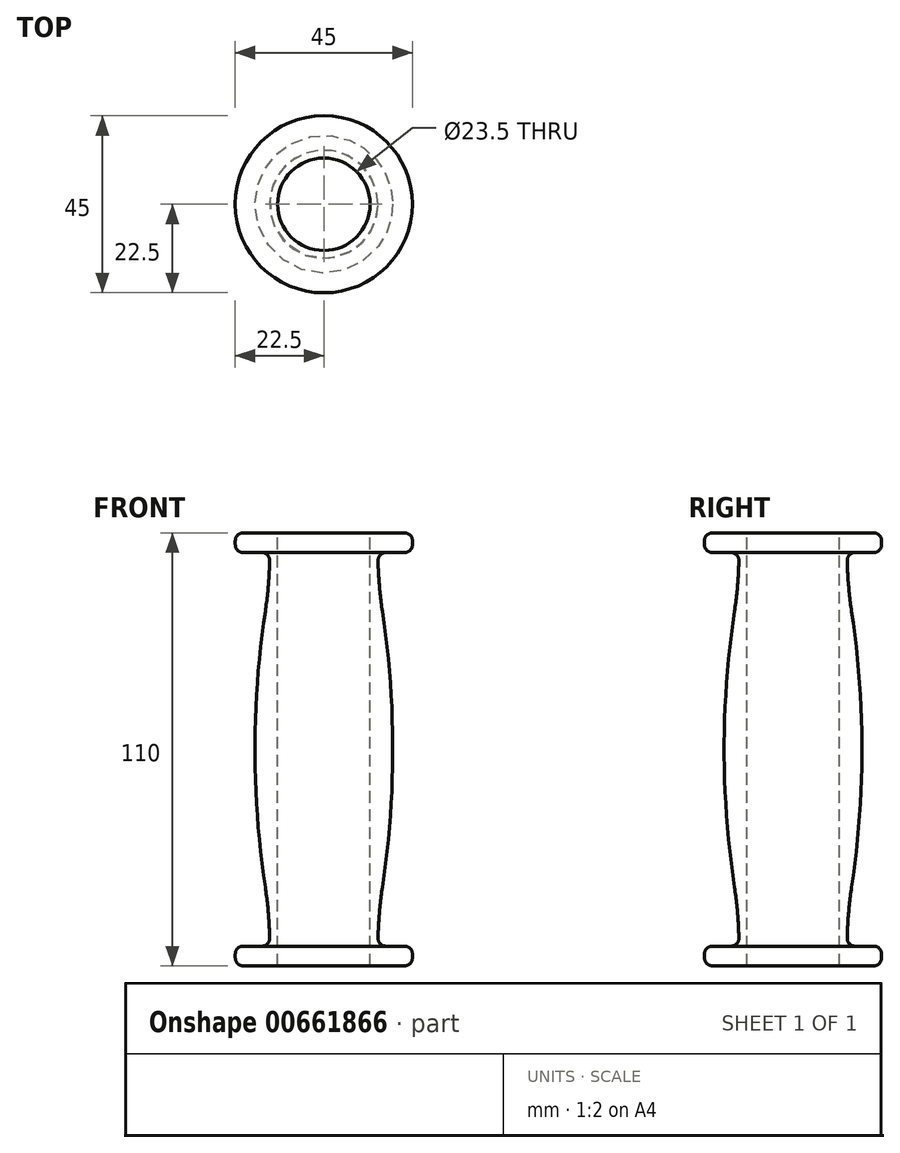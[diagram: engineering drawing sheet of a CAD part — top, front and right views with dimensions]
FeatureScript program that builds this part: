
annotation { "Feature Type Name" : "Feature", "Feature Type Description" : "" }
export const myFeature = defineFeature(function(context is Context, id is Id, definition is map)
    precondition{}
    {
        {
            var Q0;
            Q0=qCreatedBy(makeId("Right.planeOp"),FACE);
            var sketch = newSketch(context, id + "F0", { "sketchPlane" : qUnion([Q0])});
            skLineSegment(sketch, "E0", {"start": v(11.75, -55) * mm, "end": v(11.75, 55) * mm});
            skLineSegment(sketch, "E1", {"start": v(11.75, 55) * mm, "end": v(22.5, 55) * mm});
            skLineSegment(sketch, "E2", {"start": v(22.5, 55) * mm, "end": v(22.5, 50) * mm});
            skLineSegment(sketch, "E3", {"start": v(22.5, 50) * mm, "end": v(13.75, 50) * mm});
            skLineSegment(sketch, "E4", {"start": v(13.75, 50) * mm, "end": v(13.75, -50) * mm, "construction": true});
            skLineSegment(sketch, "E5", {"start": v(13.75, -50) * mm, "end": v(22.5, -50) * mm});
            skLineSegment(sketch, "E6", {"start": v(22.5, -50) * mm, "end": v(22.5, -55) * mm});
            skLineSegment(sketch, "E7", {"start": v(22.5, -55) * mm, "end": v(11.75, -55) * mm});
            skLineSegment(sketch, "E8", {"start": v(0, 0) * mm, "end": v(11.75, 0) * mm, "construction": true});
            skLineSegment(sketch, "E9", {"start": v(0, 55) * mm, "end": v(0, -55) * mm, "construction": true});
            skArc(sketch, "E10", {"start": v(13.75, 50) * mm, "mid": v(14.03, 42.52) * mm, "end": v(14.87, 35.08) * mm});
            skArc(sketch, "E11", {"start": v(14.87, -35.08) * mm, "mid": v(14.03, -42.52) * mm, "end": v(13.75, -50) * mm});
            skArc(sketch, "E12", {"start": v(14.87, -35.08) * mm, "mid": v(17.5, 0) * mm, "end": v(14.87, 35.08) * mm});
            skLineSegment(sketch, "E13", {"start": v(13.75, 0) * mm, "end": v(17.5, 0) * mm});
            skLineSegment(sketch, "E14", {"start": v(11.75, 15) * mm, "end": v(0, 15) * mm});
            skSolve(sketch);
        }
        {
            var Q0;
            Q0 = qSketchRegion(id + "F0", true);
            var Q1;
            Q1=sQuery(id+"F0.wireOp",EDGE,"E9");
            revolve(context, id + "F1", {"surfaceOperationType" : NewSurfaceOperationType.NEW, "entities" : qUnion([Q0]), "axis" : qUnion([Q1]), "revolveType" : RevolveType.FULL});
        }
        {
            var Q0;
            Q0=makeQuery(id+"F1.opRevolve","SWEPT_FACE",FACE,{"disambiguationData":[OSD([sQuery(id+"F0.wireOp",EDGE,"E2")])]});
            var Q1;
            Q1=makeQuery(id+"F1.opRevolve","SWEPT_FACE",FACE,{"disambiguationData":[OSD([sQuery(id+"F0.wireOp",EDGE,"E6")])]});
            var Q2;
            Q2=makeQuery(id+"F1.opRevolve","SWEPT_EDGE",EDGE,{"disambiguationData":[OSD([sQuery(id+"F0.wireOp",EDGE,"E3"),sQuery(id+"F0.wireOp",EDGE,"E10")])]});
            var Q3;
            Q3=makeQuery(id+"F1.opRevolve","SWEPT_EDGE",EDGE,{"disambiguationData":[OSD([sQuery(id+"F0.wireOp",EDGE,"E5"),sQuery(id+"F0.wireOp",EDGE,"E11")])]});
            fillet(context, id + "F2", {"entities" : qUnion([Q0, Q1, Q2, Q3]), "radius" : 2 * mm, "tangentPropagation" : true, "allowEdgeOverflow" : false});
        }
        {
            var Q0;
            Q0=sQuery(id+"F0.wireOp",VERTEX,"E14.end");
            var Q1;
            Q1=qCreatedBy(makeId("Top.planeOp"),FACE);
            cPlane(context, id + "F3", {"entities" : qUnion([Q0, Q1]), "cplaneType" : CPlaneType.PLANE_POINT, "offset" : 25 * mm, "width" : 150 * mm, "height" : 150 * mm});
        }
        {
            var Q0;
            Q0=qCreatedBy(id+"F3.planeOp",FACE);
            var sketch = newSketch(context, id + "F4", { "sketchPlane" : qUnion([Q0])});
            skCircle(sketch, "E15", {"center": v(0, 0) * mm, "radius": 11.75 * mm});
            skSolve(sketch);
        }
    });
